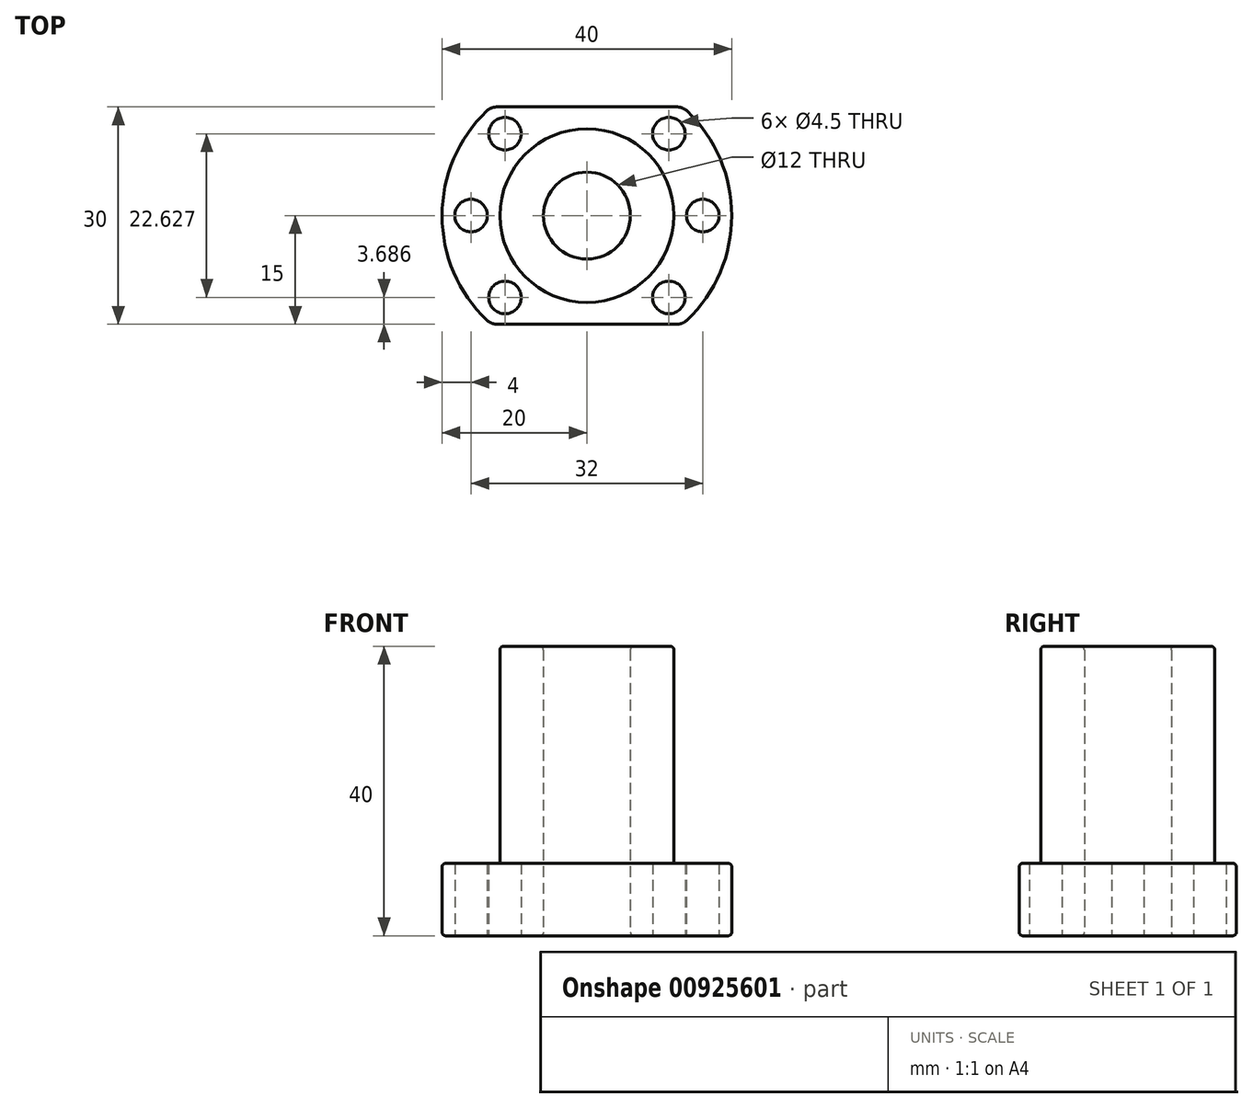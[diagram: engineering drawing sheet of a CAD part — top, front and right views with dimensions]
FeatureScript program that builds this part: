
annotation { "Feature Type Name" : "Feature", "Feature Type Description" : "" }
export const myFeature = defineFeature(function(context is Context, id is Id, definition is map)
    precondition{}
    {
        {
            var Q0;
            Q0=qCreatedBy(makeId("Top.planeOp"),FACE);
            var sketch = newSketch(context, id + "F0", { "sketchPlane" : qUnion([Q0])});
            skLineSegment(sketch, "E0.bottom", {"start": v(13.23, -15) * mm, "end": v(-13.23, -15) * mm});
            skLineSegment(sketch, "E0.top", {"start": v(13.23, 15) * mm, "end": v(-13.23, 15) * mm});
            skPoint(sketch, "E0.middle", {"position": v(0, 0) * mm});
            skArc(sketch, "E1", {"start": v(-13.23, 15) * mm, "mid": v(-20, 0) * mm, "end": v(-13.23, -15) * mm});
            skArc(sketch, "E2.trimOffspring", {"start": v(13.23, -15) * mm, "mid": v(20, 0) * mm, "end": v(13.23, 15) * mm});
            skCircle(sketch, "E3", {"center": v(0, 0) * mm, "radius": 16 * mm, "construction": true});
            skCircle(sketch, "E4", {"center": v(-16, 0) * mm, "radius": 2.25 * mm});
            skCircle(sketch, "E5.1.0", {"center": v(-11.31, 11.31) * mm, "radius": 2.25 * mm});
            skLineSegment(sketch, "E5.anchor1", {"start": v(0, 0) * mm, "end": v(-16, 0) * mm, "construction": true});
            skLineSegment(sketch, "E5.anchor2", {"start": v(0, 0) * mm, "end": v(-11.31, 11.31) * mm, "construction": true});
            skCircle(sketch, "E6.1.0", {"center": v(-11.31, -11.31) * mm, "radius": 2.25 * mm});
            skLineSegment(sketch, "E6.anchor2", {"start": v(0, 0) * mm, "end": v(-11.31, -11.31) * mm, "construction": true});
            skCircle(sketch, "E7.MirrorC", {"center": v(11.31, 11.31) * mm, "radius": 2.25 * mm});
            skCircle(sketch, "E8.MirrorC", {"center": v(16, 0) * mm, "radius": 2.25 * mm});
            skCircle(sketch, "E9.MirrorC", {"center": v(11.31, -11.31) * mm, "radius": 2.25 * mm});
            skCircle(sketch, "E10", {"center": v(0, 0) * mm, "radius": 6 * mm});
            skSolve(sketch);
        }
        {
            var Q0;
            Q0 = qSketchRegion(id + "F0", true);
            extrude(context, id + "F1", {"entities" : qUnion([Q0]), "depth" : 10 * mm, "offsetDistance" : 25 * mm});
        }
        {
            var Q0;
            Q0=makeQuery(id+"F1.opExtrude","CAP_FACE",FACE,{"disambiguationData":[OSD([sQuery(id+"F0.wireOp",EDGE,"E0.bottom"),sQuery(id+"F0.wireOp",EDGE,"E0.top"),sQuery(id+"F0.wireOp",EDGE,"E1"),sQuery(id+"F0.wireOp",EDGE,"E2.trimOffspring"),sQuery(id+"F0.wireOp",EDGE,"E4"),sQuery(id+"F0.wireOp",EDGE,"E5.1.0"),sQuery(id+"F0.wireOp",EDGE,"E6.1.0"),sQuery(id+"F0.wireOp",EDGE,"E7.MirrorC"),sQuery(id+"F0.wireOp",EDGE,"E8.MirrorC"),sQuery(id+"F0.wireOp",EDGE,"E9.MirrorC"),sQuery(id+"F0.wireOp",EDGE,"E10")])],"isStart":false});
            var sketch = newSketch(context, id + "F2", { "sketchPlane" : qUnion([Q0])});
            skCircle(sketch, "E11", {"center": v(0, 0) * mm, "radius": 12 * mm});
            skCircle(sketch, "E12.0", {"center": v(0, 0) * mm, "radius": 6 * mm});
            skSolve(sketch);
        }
        {
            var Q0;
            Q0 = qSketchRegion(id + "F2", true);
            extrude(context, id + "F3", {"entities" : qUnion([Q0]), "operationType" : NewBodyOperationType.ADD, "depth" : 30 * mm, "offsetDistance" : 25 * mm});
        }
        {
            var Q0;
            Q0=makeQuery(id+"F1.opExtrude","SWEPT_EDGE",EDGE,{"disambiguationData":[OSD([sQuery(id+"F0.wireOp",EDGE,"E0.bottom"),sQuery(id+"F0.wireOp",EDGE,"E1")])]});
            var Q1;
            Q1=makeQuery(id+"F1.opExtrude","SWEPT_EDGE",EDGE,{"disambiguationData":[OSD([sQuery(id+"F0.wireOp",EDGE,"E0.bottom"),sQuery(id+"F0.wireOp",EDGE,"E2.trimOffspring")])]});
            var Q2;
            Q2=makeQuery(id+"F1.opExtrude","SWEPT_EDGE",EDGE,{"disambiguationData":[OSD([sQuery(id+"F0.wireOp",EDGE,"E0.top"),sQuery(id+"F0.wireOp",EDGE,"E2.trimOffspring")])]});
            var Q3;
            Q3=makeQuery(id+"F1.opExtrude","SWEPT_EDGE",EDGE,{"disambiguationData":[OSD([sQuery(id+"F0.wireOp",EDGE,"E0.top"),sQuery(id+"F0.wireOp",EDGE,"E1")])]});
            fillet(context, id + "F4", {"entities" : qUnion([Q0, Q1, Q2, Q3]), "radius" : 2 * mm, "tangentPropagation" : true, "allowEdgeOverflow" : false});
        }
        {
            var Q0;
            Q0=makeQuery(id+"F3.opExtrude","CAP_EDGE",EDGE,{"disambiguationData":[OSD([sQuery(id+"F2.wireOp",EDGE,"E11")])],"isStart":false});
            var Q1;
            Q1=makeQuery(id+"F1.opExtrude","CAP_EDGE",EDGE,{"disambiguationData":[OSD([sQuery(id+"F0.wireOp",EDGE,"E2.trimOffspring")])],"isStart":false});
            var Q2;
            Q2=makeQuery(id+"F1.opExtrude","CAP_EDGE",EDGE,{"disambiguationData":[OSD([sQuery(id+"F0.wireOp",EDGE,"E2.trimOffspring")])],"isStart":true});
            var Q3;
            Q3=makeQuery(id+"F3.opExtrude","CAP_EDGE",EDGE,{"disambiguationData":[OSD([sQuery(id+"F2.wireOp",EDGE,"E12.0")])],"isStart":false});
            var Q4;
            Q4=makeQuery(id+"F1.opExtrude","CAP_EDGE",EDGE,{"disambiguationData":[OSD([sQuery(id+"F0.wireOp",EDGE,"E10")])],"isStart":true});
            fillet(context, id + "F5", {"entities" : qUnion([Q0, Q1, Q2, Q3, Q4]), "radius" : .5 * mm, "tangentPropagation" : true, "allowEdgeOverflow" : false});
        }
    });
